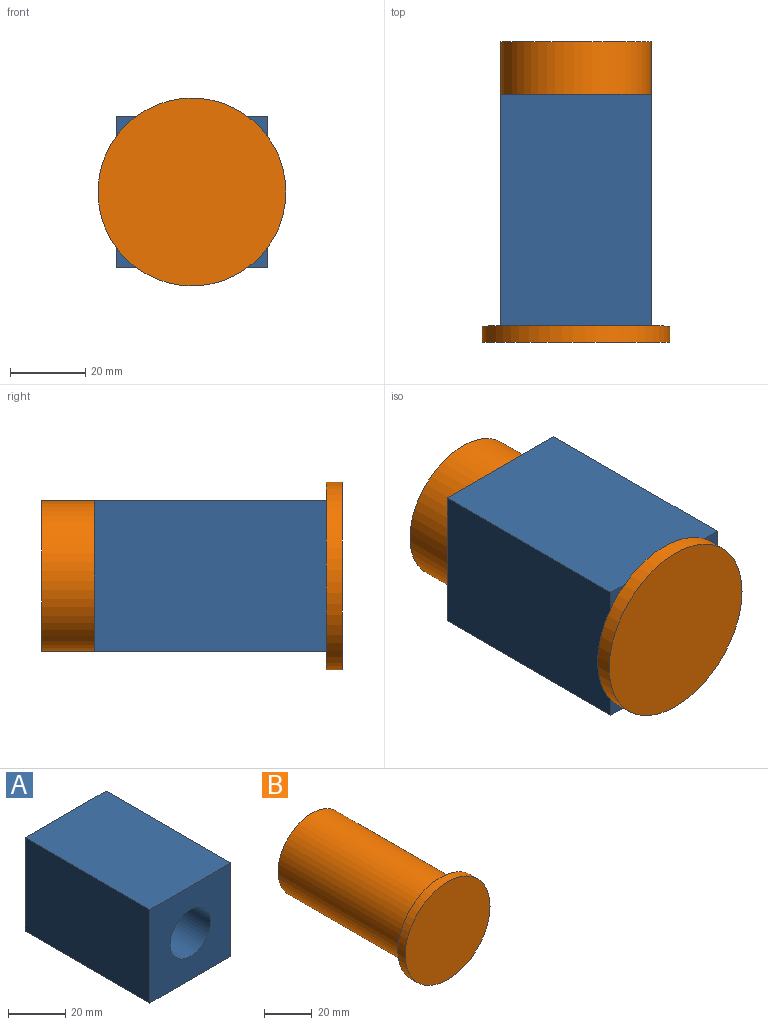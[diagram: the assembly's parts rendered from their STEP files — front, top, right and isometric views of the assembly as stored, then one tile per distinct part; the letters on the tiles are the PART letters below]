
ASSEMBLY  parts=2 mates=2
PART A: 7 faces, bbox 40x61.7x40 mm
  f0: plane 61.7x40mm, normal (0,0,-1), area 2468mm2, adj f1,f4,f5,f6
  f1: plane 61.7x40mm, normal (1,0,0), area 2468mm2, adj f0,f2,f5,f6
  f2: plane 61.7x40mm, normal (0,0,1), area 2468mm2, adj f1,f4,f5,f6
  f3: cylinder r=10mm len=61.7mm, axis (0,1,0), area 3876.7mm2, adj f5,f6
  f4: plane 61.7x40mm, normal (-1,0,0), area 2468mm2, adj f0,f2,f5,f6
  f5: plane 40x40mm, normal (0,-1,0), area 1285.8mm2, adj f0,f1,f2,f3,f4
  f6: plane 40x40mm, normal (0,1,0), area 1285.8mm2, adj f0,f1,f2,f3,f4
PART B: 5 faces, bbox 50x80x50 mm
  f0: cylinder r=20mm len=75.68mm, axis (0,1,0), area 9510.7mm2, adj f1,f3
  f1: plane 40x40mm, normal (0,1,0), area 1256.6mm2, adj f0
  f2: cylinder r=25mm len=50mm, axis (0,-1,0), area 678mm2, adj f3,f4
  f3: plane 50x50mm, normal (0,1,0), area 706.9mm2, adj f0,f2
  f4: plane 50x50mm, normal (0,-1,0), area 1963.5mm2, adj f2
PLACE A t=(6.78,95.3,14.29)mm fixed
PLACE B t=(6.78,109.28,14.29)mm
MATE cylindrical B.f0 <-> A.f3  axis (0,1,0) through (6.78,71.44,14.29)mm
MATE planar B.f0 <-> A.f3  axis (0,1,0) through (6.78,33.6,14.29)mm
